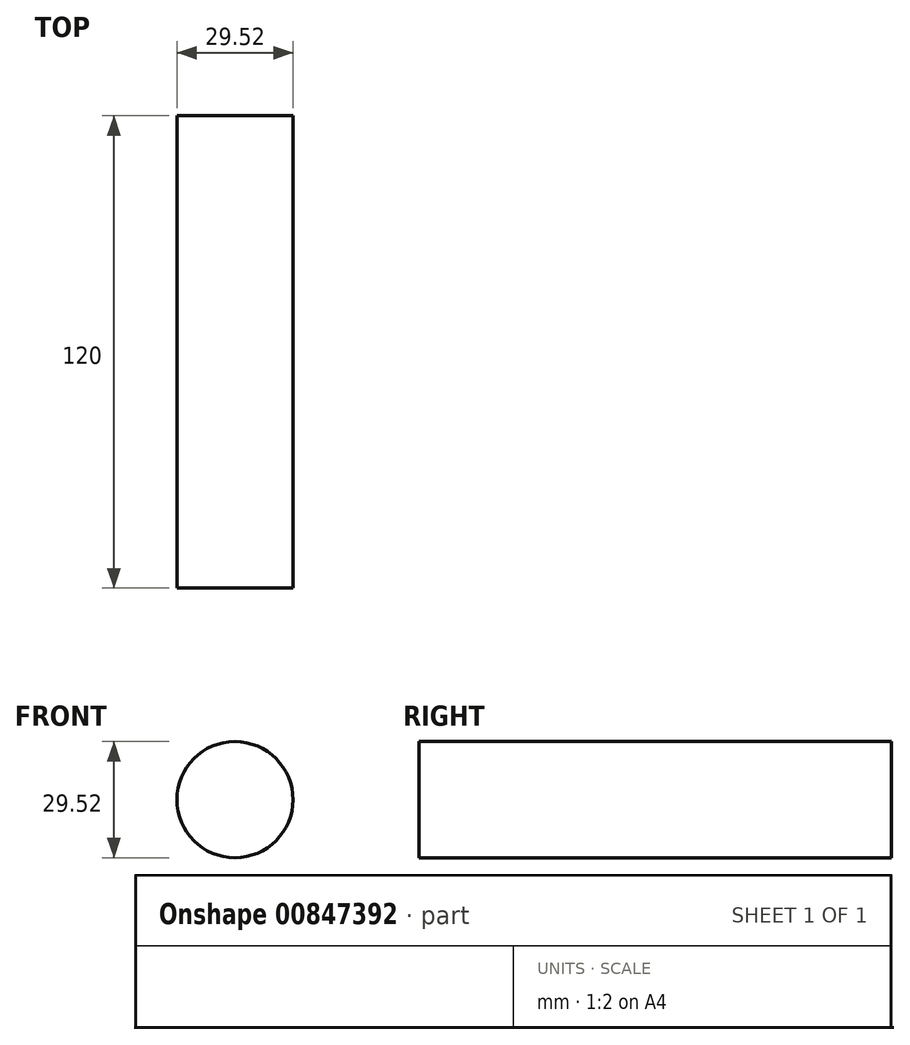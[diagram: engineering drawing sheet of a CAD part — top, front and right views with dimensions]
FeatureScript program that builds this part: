
annotation { "Feature Type Name" : "Feature", "Feature Type Description" : "" }
export const myFeature = defineFeature(function(context is Context, id is Id, definition is map)
    precondition{}
    {
        {
            var Q0;
            Q0=qCreatedBy(makeId("Front.planeOp"),FACE);
            var sketch = newSketch(context, id + "F0", { "sketchPlane" : qUnion([Q0])});
            skCircle(sketch, "E0", {"center": v(0, 0) * mm, "radius": 14.76 * mm});
            skSolve(sketch);
        }
        {
            var Q0;
            Q0 = qSketchRegion(id + "F0", true);
            extrude(context, id + "F1", {"entities" : qUnion([Q0]), "depth" : 120 * mm, "offsetDistance" : 25 * mm});
        }
    });
